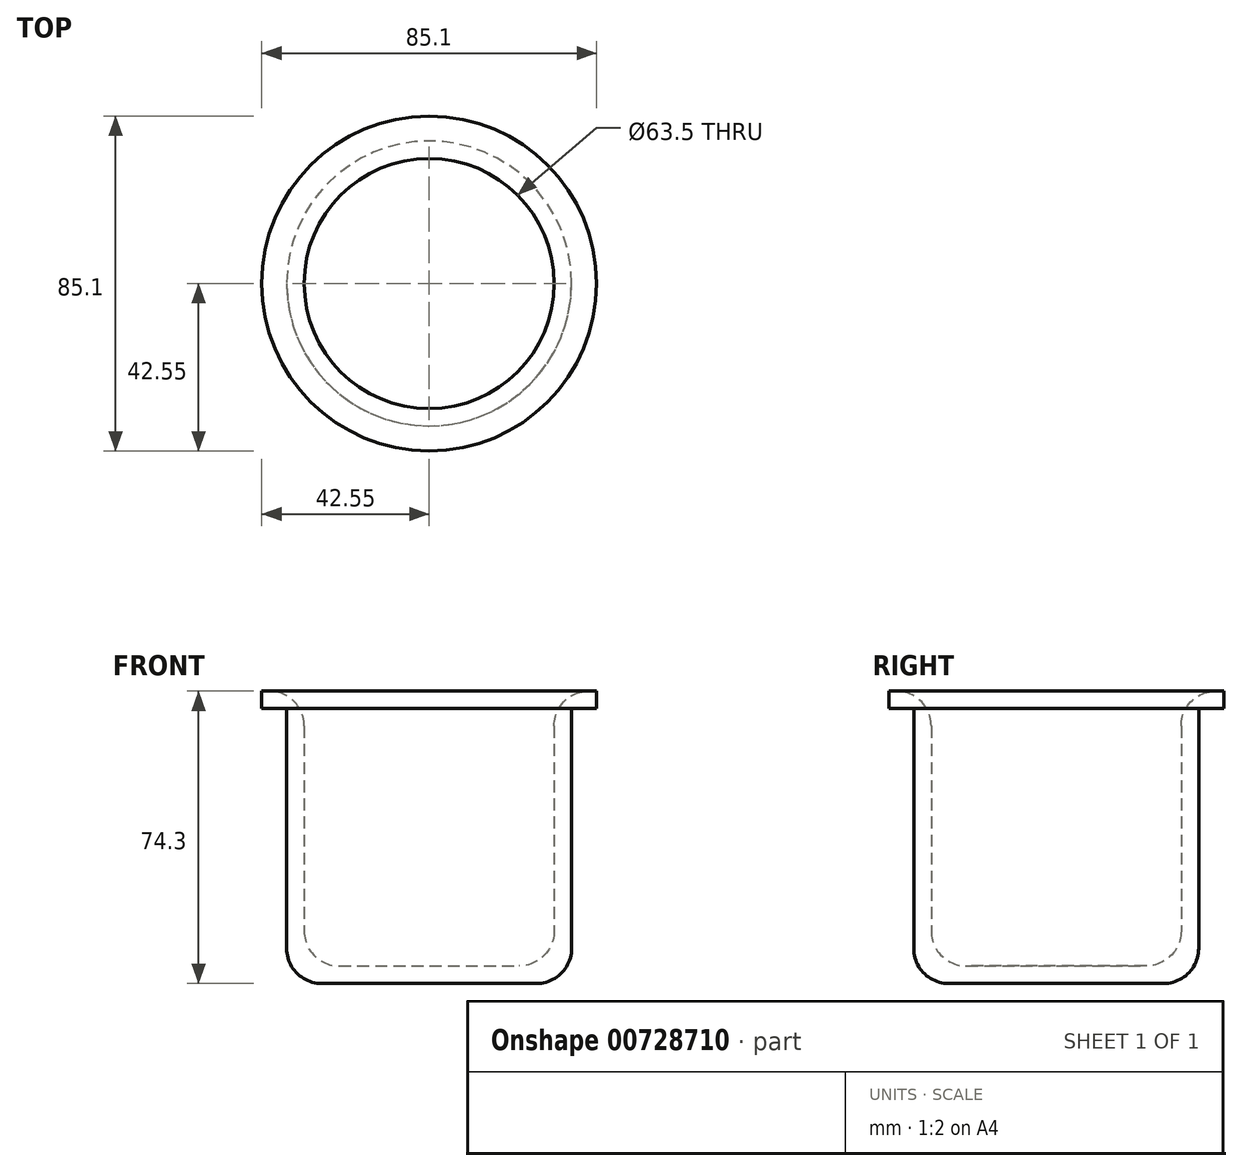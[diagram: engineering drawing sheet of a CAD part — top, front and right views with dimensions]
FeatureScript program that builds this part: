
annotation { "Feature Type Name" : "Feature", "Feature Type Description" : "" }
export const myFeature = defineFeature(function(context is Context, id is Id, definition is map)
    precondition{}
    {
        {
            var Q0;
            Q0=qCreatedBy(makeId("Front.planeOp"),FACE);
            var sketch = newSketch(context, id + "F0", { "sketchPlane" : qUnion([Q0])});
            skLineSegment(sketch, "E0", {"start": v(31.75, 74.3) * mm, "end": v(42.55, 74.3) * mm});
            skLineSegment(sketch, "E1", {"start": v(42.55, 74.3) * mm, "end": v(42.55, 69.85) * mm});
            skLineSegment(sketch, "E2", {"start": v(42.55, 69.85) * mm, "end": v(36.2, 69.85) * mm});
            skLineSegment(sketch, "E3", {"start": v(36.2, 69.85) * mm, "end": v(36.2, 0) * mm});
            skLineSegment(sketch, "E4", {"start": v(36.2, 0) * mm, "end": v(0, 0) * mm});
            skLineSegment(sketch, "E5", {"start": v(0, 0) * mm, "end": v(0, 4.44) * mm});
            skLineSegment(sketch, "E6", {"start": v(0, 4.44) * mm, "end": v(31.75, 4.45) * mm});
            skLineSegment(sketch, "E7", {"start": v(31.75, 4.45) * mm, "end": v(31.75, 74.3) * mm});
            skLineSegment(sketch, "E8", {"start": v(38.1, 15.4) * mm, "end": v(38.1, 61.55) * mm, "construction": true});
            skSolve(sketch);
        }
        {
            var Q0;
            Q0 = qSketchRegion(id + "F0", true);
            var Q1;
            Q1=sQuery(id+"F0.wireOp",EDGE,"E5");
            revolve(context, id + "F1", {"surfaceOperationType" : NewSurfaceOperationType.NEW, "entities" : qUnion([Q0]), "axis" : qUnion([Q1]), "revolveType" : RevolveType.FULL});
        }
        {
            var Q0;
            Q0=makeQuery(id+"F1.opRevolve","SWEPT_EDGE",EDGE,{"disambiguationData":[OSD([sQuery(id+"F0.wireOp",EDGE,"E0"),sQuery(id+"F0.wireOp",EDGE,"E7")])]});
            var Q1;
            Q1=makeQuery(id+"F1.opRevolve","SWEPT_EDGE",EDGE,{"disambiguationData":[OSD([sQuery(id+"F0.wireOp",EDGE,"E6"),sQuery(id+"F0.wireOp",EDGE,"E7")])]});
            var Q2;
            Q2=makeQuery(id+"F1.opRevolve","SWEPT_EDGE",EDGE,{"disambiguationData":[OSD([sQuery(id+"F0.wireOp",EDGE,"E3"),sQuery(id+"F0.wireOp",EDGE,"E4")])]});
            fillet(context, id + "F2", {"entities" : qUnion([Q0, Q1, Q2]), "radius" : 8.9 * mm, "tangentPropagation" : true, "allowEdgeOverflow" : false});
        }
    });
